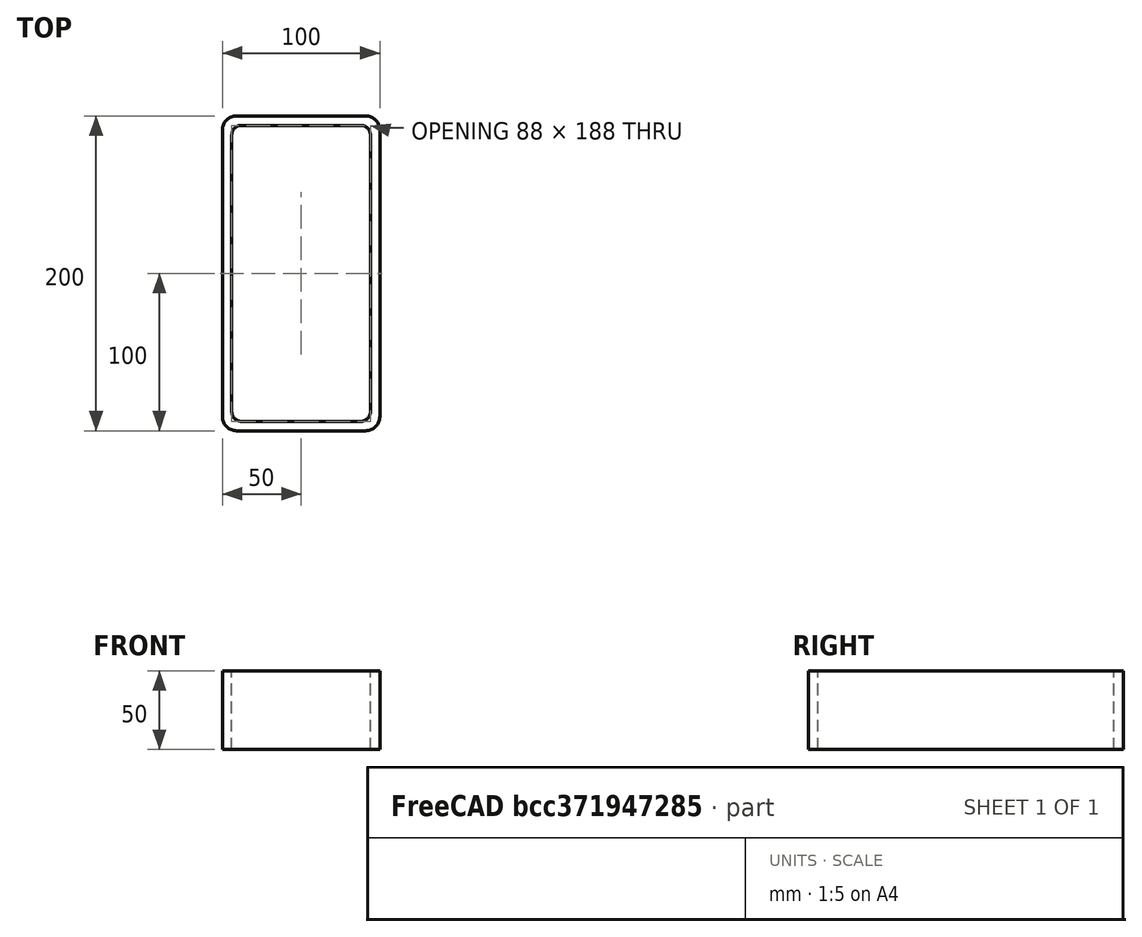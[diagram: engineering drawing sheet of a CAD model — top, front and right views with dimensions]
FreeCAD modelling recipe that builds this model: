
FCSTD DOCUMENT  (FreeCAD 0.15R4671 (Git))
Label: Rectangular hollow section 200x100x6 EN10219 S235JRH
License: All rights reserved
LicenseURL: http://en.wikipedia.org/wiki/All_rights_reserved
objects: Sketcher::SketchObject×1, Part::Extrusion×1
note: 2 computed .brp shape members not serialized (recipe doc carries the construction recipe); baked Part::Feature solids carry a one-line shape summary decoded from their .brp

FEATURE [Sketcher::SketchObject] Sketch
  sketch-geometry (16):
    g0: LineSegment StartX=-38 StartY=94 StartZ=0 EndX=38 EndY=94 EndZ=0
    g1: LineSegment StartX=44 StartY=88 StartZ=0 EndX=44 EndY=-88 EndZ=0
    g2: LineSegment StartX=38 StartY=-94 StartZ=0 EndX=-38 EndY=-94 EndZ=0
    g3: LineSegment StartX=-44 StartY=-88 StartZ=0 EndX=-44 EndY=88 EndZ=0
    g4: LineSegment StartX=-41 StartY=100 StartZ=0 EndX=41 EndY=100 EndZ=0
    g5: LineSegment StartX=50 StartY=91 StartZ=0 EndX=50 EndY=-91 EndZ=0
    g6: LineSegment StartX=41 StartY=-100 StartZ=0 EndX=-41 EndY=-100 EndZ=0
    g7: LineSegment StartX=-50 StartY=-91 StartZ=0 EndX=-50 EndY=91 EndZ=0
    g8: ArcOfCircle CenterX=-38 CenterY=88 CenterZ=0 NormalX=0 NormalY=0 NormalZ=1 Radius=6 StartAngle=1.5708 EndAngle=3.14159
    g9: ArcOfCircle CenterX=38 CenterY=88 CenterZ=0 NormalX=0 NormalY=0 NormalZ=1 Radius=6 StartAngle=0 EndAngle=1.5708
    g10: ArcOfCircle CenterX=38 CenterY=-88 CenterZ=0 NormalX=0 NormalY=0 NormalZ=1 Radius=6 StartAngle=4.71239 EndAngle=6.28319
    g11: ArcOfCircle CenterX=-38 CenterY=-88 CenterZ=0 NormalX=0 NormalY=0 NormalZ=1 Radius=6 StartAngle=3.14159 EndAngle=4.71239
    g12: ArcOfCircle CenterX=41 CenterY=91 CenterZ=0 NormalX=0 NormalY=0 NormalZ=1 Radius=9 StartAngle=0 EndAngle=1.5708
    g13: ArcOfCircle CenterX=41 CenterY=-91 CenterZ=0 NormalX=0 NormalY=0 NormalZ=1 Radius=9 StartAngle=4.71239 EndAngle=6.28319
    g14: ArcOfCircle CenterX=-41 CenterY=-91 CenterZ=0 NormalX=0 NormalY=0 NormalZ=1 Radius=9 StartAngle=3.14159 EndAngle=4.71239
    g15: ArcOfCircle CenterX=-41 CenterY=91 CenterZ=0 NormalX=0 NormalY=0 NormalZ=1 Radius=9 StartAngle=1.5708 EndAngle=3.14159
  constraints (36):
    c: Horizontal(g2)
    c: Vertical(g3)
    c: Horizontal(g6)
    c: Vertical(g7)
    c: Tangent(g3,g8) = 1.5708
    c: Tangent(g0,g8) = 1.5708
    c: Tangent(g0,g9) = 1.5708
    c: Tangent(g1,g9) = 1.5708
    c: Tangent(g1,g10) = 1.5708
    c: Tangent(g2,g10) = 1.5708
    c: Tangent(g2,g11) = 1.5708
    c: Tangent(g3,g11) = 1.5708
    c: Tangent(g4,g12) = 1.5708
    c: Tangent(g5,g12) = 1.5708
    c: Tangent(g5,g13) = 1.5708
    c: Tangent(g6,g13) = 1.5708
    c: Tangent(g6,g14) = 1.5708
    c: Tangent(g7,g14) = 1.5708
    c: Tangent(g7,g15) = 1.5708
    c: Tangent(g4,g15) = 1.5708
    c: Equal(g9,g8)
    c: Equal(g9,g11)
    c: Equal(g9,g10)
    c: Equal(g12,g15)
    c: Equal(g12,g14)
    c: Equal(g12,g13)
    c: Symmetric(g4,g6,g-1)
    c: Symmetric(g7,g5,g-2)
    c: DistanceY(g4,g6) = -200
    c: DistanceX(g7,g5) = 100
    c: Symmetric(g3,g1,g-2)
    c: Symmetric(g0,g2,g-1)
    c: DistanceY(g0,g4) = 6
    c: DistanceX(g5,g1) = -6
    c: Radius(g9) = 6
    c: Radius(g12) = 9
FEATURE [Part::Extrusion] Extrude  label="Rectangular hollow section 200x100x6 EN10219 S235JRH"
  Base = -> Sketch
  Dir = (0,0,50)
  Solid = true
